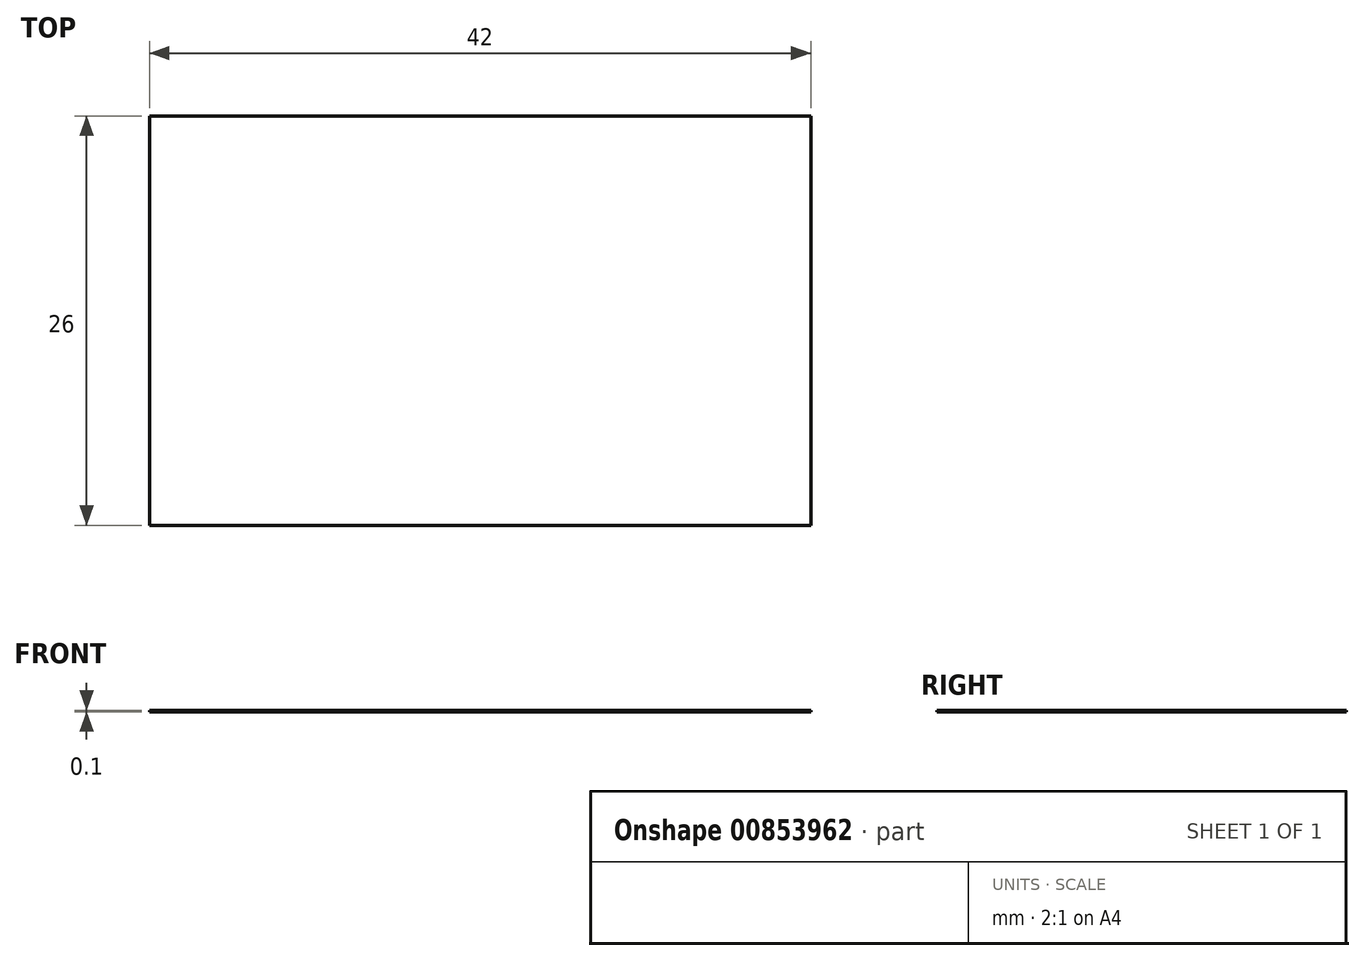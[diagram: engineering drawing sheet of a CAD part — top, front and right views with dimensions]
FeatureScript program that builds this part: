
annotation { "Feature Type Name" : "Feature", "Feature Type Description" : "" }
export const myFeature = defineFeature(function(context is Context, id is Id, definition is map)
    precondition{}
    {
        {
            var Q0;
            Q0=qCreatedBy(makeId("Top.planeOp"),FACE);
            var sketch = newSketch(context, id + "F0", { "sketchPlane" : qUnion([Q0])});
            skLineSegment(sketch, "E0.bottom", {"start": v(0, 0) * mm, "end": v(42, 0) * mm});
            skLineSegment(sketch, "E0.top", {"start": v(0, 26) * mm, "end": v(42, 26) * mm});
            skLineSegment(sketch, "E0.left", {"start": v(0, 0) * mm, "end": v(0, 26) * mm});
            skLineSegment(sketch, "E0.right", {"start": v(42, 0) * mm, "end": v(42, 26) * mm});
            skSolve(sketch);
        }
        {
            var Q0;
            Q0 = qSketchRegion(id + "F0", true);
            extrude(context, id + "F1", {"entities" : qUnion([Q0]), "depth" : 0.1 * mm, "offsetDistance" : 25 * mm});
        }
    });
